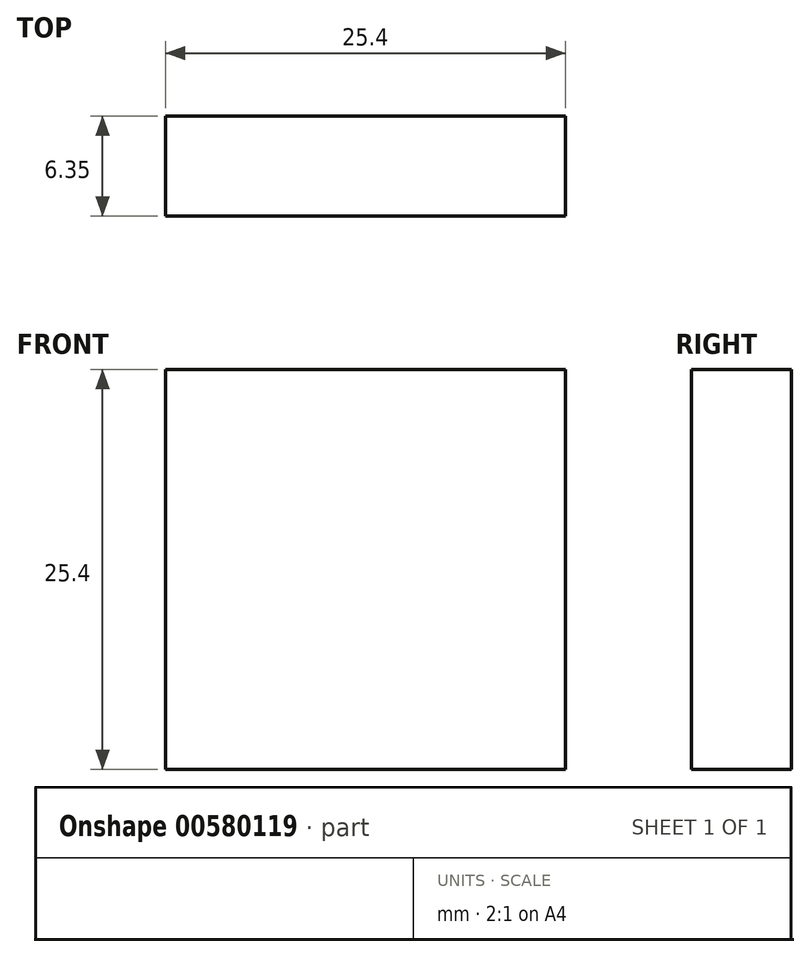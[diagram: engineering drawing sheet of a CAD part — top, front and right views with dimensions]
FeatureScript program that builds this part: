
annotation { "Feature Type Name" : "Feature", "Feature Type Description" : "" }
export const myFeature = defineFeature(function(context is Context, id is Id, definition is map)
    precondition{}
    {
        {
            var Q0;
            Q0=qCreatedBy(makeId("Front.planeOp"),FACE);
            var sketch = newSketch(context, id + "F0", { "sketchPlane" : qUnion([Q0])});
            skLineSegment(sketch, "E0.bottom", {"start": v(-9.3, 8.1) * mm, "end": v(16.1, 8.1) * mm});
            skLineSegment(sketch, "E0.top", {"start": v(-9.3, -17.3) * mm, "end": v(16.1, -17.3) * mm});
            skLineSegment(sketch, "E0.left", {"start": v(-9.3, 8.1) * mm, "end": v(-9.3, -17.3) * mm});
            skLineSegment(sketch, "E0.right", {"start": v(16.1, 8.1) * mm, "end": v(16.1, -17.3) * mm});
            skSolve(sketch);
        }
        {
            var Q0;
            Q0 = qSketchRegion(id + "F0", true);
            extrude(context, id + "F1", {"entities" : qUnion([Q0]), "depth" : 6.35 * mm, "offsetDistance" : 25.4 * mm});
        }
    });
